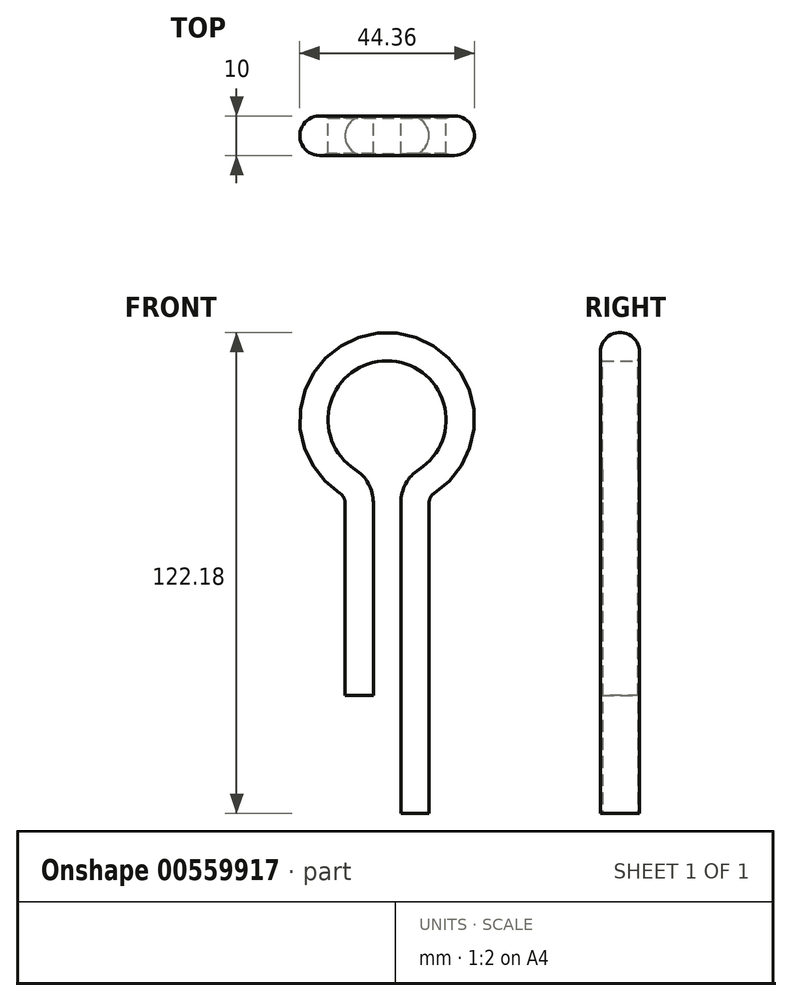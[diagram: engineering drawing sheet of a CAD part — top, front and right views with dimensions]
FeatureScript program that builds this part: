
annotation { "Feature Type Name" : "Feature", "Feature Type Description" : "" }
export const myFeature = defineFeature(function(context is Context, id is Id, definition is map)
    precondition{}
    {
        {
            var Q0;
            Q0=qCreatedBy(makeId("Front.planeOp"),FACE);
            var sketch = newSketch(context, id + "F0", { "sketchPlane" : qUnion([Q0])});
            skLineSegment(sketch, "E0", {"start": v(-3.5, -21.04) * mm, "end": v(-3.5, -70) * mm});
            skLineSegment(sketch, "E1", {"start": v(3.5, -21.04) * mm, "end": v(3.5, -100) * mm});
            skArc(sketch, "E2", {"start": v(-8.1, -12.62) * mm, "mid": v(0, 15) * mm, "end": v(8.1, -12.62) * mm});
            skPoint(sketch, "E3.visualSharp", {"position": v(-3.5, -14.59) * mm});
            skArc(sketch, "E3.filletArc", {"start": v(-3.5, -21.04) * mm, "mid": v(-4.73, -16.25) * mm, "end": v(-8.1, -12.62) * mm});
            skPoint(sketch, "E4.visualSharp", {"position": v(3.5, -14.59) * mm});
            skArc(sketch, "E4.filletArc", {"start": v(8.1, -12.62) * mm, "mid": v(4.73, -16.25) * mm, "end": v(3.5, -21.04) * mm});
            skSolve(sketch);
        }
        {
            var Q0;
            Q0=qCreatedBy(makeId("Top.planeOp"),FACE);
            cPlane(context, id + "F1", {"entities" : qUnion([Q0]), "cplaneType" : CPlaneType.OFFSET, "offset" : 70 * mm, "oppositeDirection" : true, "width" : 150 * mm, "height" : 150 * mm});
        }
        {
            var Q0;
            Q0=qCreatedBy(id+"F1.planeOp",FACE);
            var sketch = newSketch(context, id + "F2", { "sketchPlane" : qUnion([Q0])});
            skArc(sketch, "E5", {"start": v(-3.5, 4.5) * mm, "mid": v(-10.68, 0) * mm, "end": v(-3.5, -4.5) * mm});
            skLineSegment(sketch, "E6", {"start": v(-3.5, -4.5) * mm, "end": v(-3.5, 4.5) * mm});
            skSolve(sketch);
        }
        {
            var Q0;
            Q0=makeQuery(id+"F2.imprint","IMPRINT",FACE,{"disambiguationData":[TD([[makeQuery(id+"F2.imprint","IMPRINT",EDGE,{"derivedFrom":sQuery(id+"F2.wireOp",EDGE,"E5")}),1.0]])]});
            var Q1;
            Q1 = qConstructionFilter(qBodyType(qCreatedBy(id + "F0" ,EDGE), BodyType.WIRE), ConstructionObject.NO);
            sweep(context, id + "F3", {"profiles" : qUnion([Q0]), "path" : qUnion([Q1])});
        }
    });
